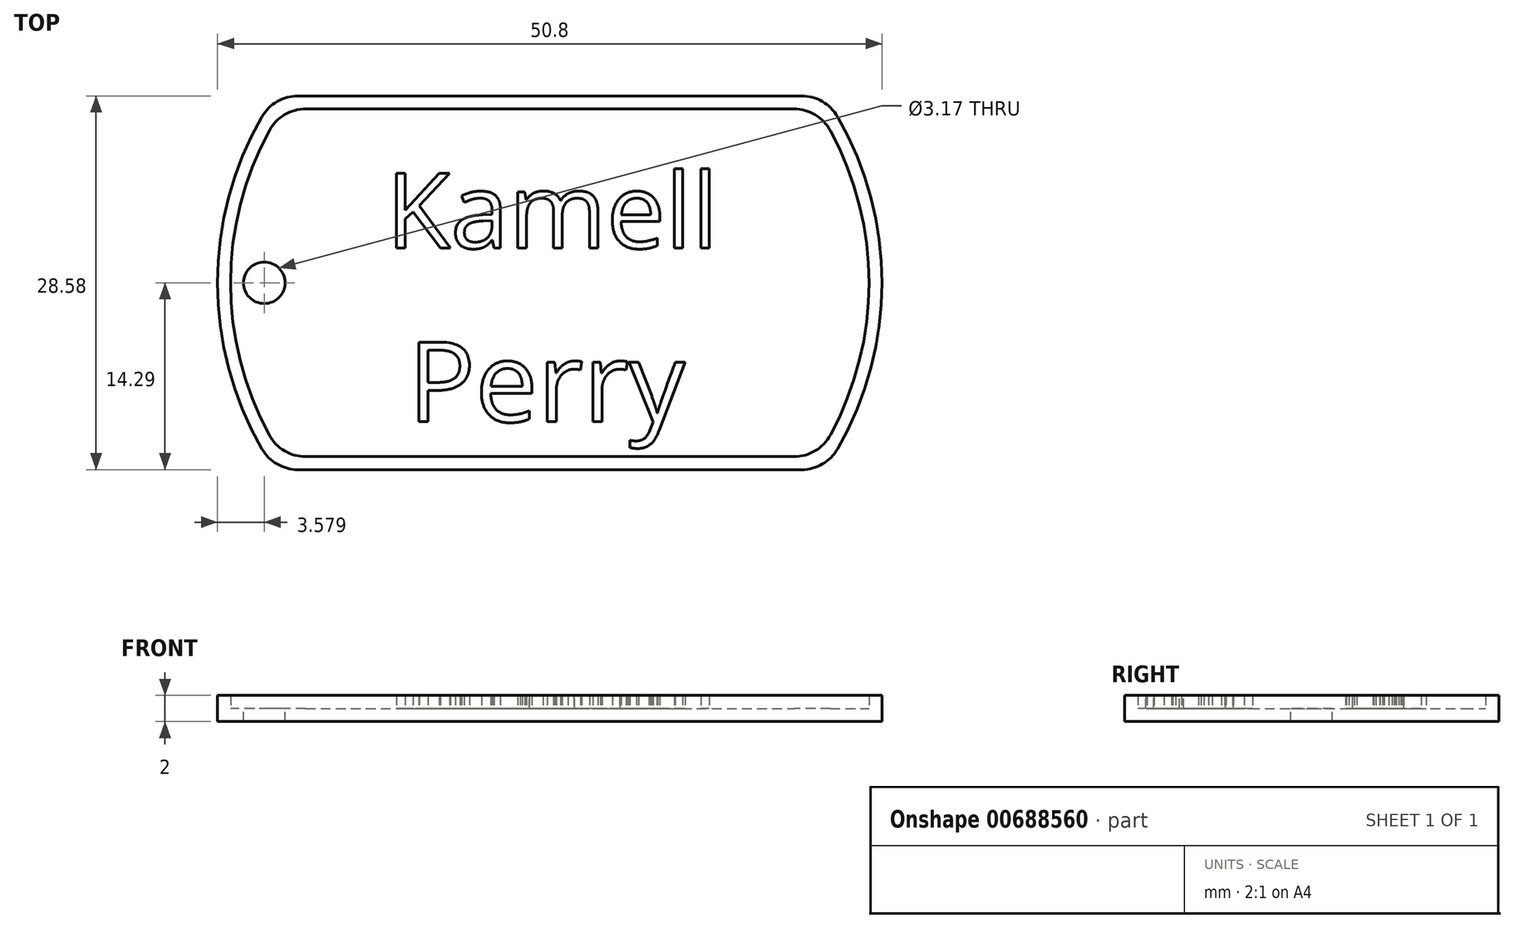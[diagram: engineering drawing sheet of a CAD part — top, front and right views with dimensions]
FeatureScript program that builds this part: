
annotation { "Feature Type Name" : "Feature", "Feature Type Description" : "" }
export const myFeature = defineFeature(function(context is Context, id is Id, definition is map)
    precondition{}
    {
        {
            var Q0;
            Q0=qCreatedBy(makeId("Top.planeOp"),FACE);
            var sketch = newSketch(context, id + "F0", { "sketchPlane" : qUnion([Q0])});
            skArc(sketch, "E0", {"start": v(-22, 12.7) * mm, "mid": v(-25.4, 0) * mm, "end": v(-22, -12.7) * mm});
            skLineSegment(sketch, "E1.top", {"start": v(-19.25, -14.29) * mm, "end": v(19.25, -14.29) * mm});
            skArc(sketch, "E2.trimOffspring", {"start": v(22, -12.7) * mm, "mid": v(25.4, 0) * mm, "end": v(22, 12.7) * mm});
            skLineSegment(sketch, "E3", {"start": v(-19.25, 14.29) * mm, "end": v(19.25, 14.29) * mm});
            skPoint(sketch, "E4.visualSharp", {"position": v(-21, 14.29) * mm});
            skArc(sketch, "E4.filletArc", {"start": v(-19.25, 14.29) * mm, "mid": v(-20.83, 13.86) * mm, "end": v(-22, 12.7) * mm});
            skPoint(sketch, "E5.visualSharp", {"position": v(21, 14.29) * mm});
            skArc(sketch, "E5.filletArc", {"start": v(22, 12.7) * mm, "mid": v(20.83, 13.86) * mm, "end": v(19.25, 14.29) * mm});
            skPoint(sketch, "E6.visualSharp", {"position": v(21, -14.29) * mm});
            skArc(sketch, "E6.filletArc", {"start": v(19.25, -14.29) * mm, "mid": v(20.83, -13.86) * mm, "end": v(22, -12.7) * mm});
            skPoint(sketch, "E7.visualSharp", {"position": v(-21, -14.29) * mm});
            skArc(sketch, "E7.filletArc", {"start": v(-22, -12.7) * mm, "mid": v(-20.83, -13.86) * mm, "end": v(-19.25, -14.29) * mm});
            skSolve(sketch);
        }
        {
            var Q0;
            Q0=makeQuery(id+"F0.imprint","IMPRINT",FACE,{"disambiguationData":[TD([[makeQuery(id+"F0.imprint","IMPRINT",EDGE,{"derivedFrom":sQuery(id+"F0.wireOp",EDGE,"E0")}),1.0]])]});
            extrude(context, id + "F1", {"entities" : qUnion([Q0]), "depth" : 1 * mm, "offsetDistance" : 25.4 * mm});
        }
        {
            var Q0;
            Q0=makeQuery(id+"F1.opExtrude","CAP_FACE",FACE,{"disambiguationData":[OSD([sQuery(id+"F0.wireOp",EDGE,"E0"),sQuery(id+"F0.wireOp",EDGE,"E1.top"),sQuery(id+"F0.wireOp",EDGE,"E2.trimOffspring"),sQuery(id+"F0.wireOp",EDGE,"E3"),sQuery(id+"F0.wireOp",EDGE,"E4.filletArc"),sQuery(id+"F0.wireOp",EDGE,"E5.filletArc"),sQuery(id+"F0.wireOp",EDGE,"E6.filletArc"),sQuery(id+"F0.wireOp",EDGE,"E7.filletArc")])],"isStart":false});
            var sketch = newSketch(context, id + "F2", { "sketchPlane" : qUnion([Q0])});
            skLineSegment(sketch, "E8.0", {"start": v(-18.66, 13.29) * mm, "end": v(18.66, 13.29) * mm});
            skArc(sketch, "E8.1", {"start": v(-21.45, 11.63) * mm, "mid": v(-24.4, 0) * mm, "end": v(-21.45, -11.63) * mm});
            skLineSegment(sketch, "E8.2", {"start": v(-18.66, -13.29) * mm, "end": v(18.66, -13.29) * mm});
            skArc(sketch, "E8.3", {"start": v(21.45, -11.63) * mm, "mid": v(24.4, 0) * mm, "end": v(21.45, 11.63) * mm});
            skPoint(sketch, "E9.visualSharp", {"position": v(-20.46, 13.29) * mm});
            skArc(sketch, "E9.filletArc", {"start": v(-18.66, 13.29) * mm, "mid": v(-20.29, 12.84) * mm, "end": v(-21.45, 11.63) * mm});
            skPoint(sketch, "E10.visualSharp", {"position": v(20.46, 13.29) * mm});
            skArc(sketch, "E10.filletArc", {"start": v(21.45, 11.63) * mm, "mid": v(20.29, 12.84) * mm, "end": v(18.66, 13.29) * mm});
            skPoint(sketch, "E11.visualSharp", {"position": v(20.46, -13.29) * mm});
            skArc(sketch, "E11.filletArc", {"start": v(18.66, -13.29) * mm, "mid": v(20.29, -12.84) * mm, "end": v(21.45, -11.63) * mm});
            skPoint(sketch, "E12.visualSharp", {"position": v(-20.46, -13.29) * mm});
            skArc(sketch, "E12.filletArc", {"start": v(-21.45, -11.63) * mm, "mid": v(-20.29, -12.84) * mm, "end": v(-18.66, -13.29) * mm});
            skLineSegment(sketch, "E13.0", {"start": v(-19.25, 14.29) * mm, "end": v(19.25, 14.29) * mm});
            skArc(sketch, "E13.1", {"start": v(-22, 12.7) * mm, "mid": v(-25.4, 0) * mm, "end": v(-22, -12.7) * mm});
            skLineSegment(sketch, "E13.2", {"start": v(-19.25, -14.29) * mm, "end": v(19.25, -14.29) * mm});
            skArc(sketch, "E13.3", {"start": v(22, -12.7) * mm, "mid": v(25.4, 0) * mm, "end": v(22, 12.7) * mm});
            skPoint(sketch, "E14.visualSharp", {"position": v(-21, -14.29) * mm});
            skArc(sketch, "E14.filletArc", {"start": v(-22, -12.7) * mm, "mid": v(-20.83, -13.86) * mm, "end": v(-19.25, -14.29) * mm});
            skPoint(sketch, "E15.visualSharp", {"position": v(21, -14.29) * mm});
            skArc(sketch, "E15.filletArc", {"start": v(19.25, -14.29) * mm, "mid": v(20.83, -13.86) * mm, "end": v(22, -12.7) * mm});
            skPoint(sketch, "E16.visualSharp", {"position": v(21, 14.29) * mm});
            skArc(sketch, "E16.filletArc", {"start": v(22, 12.7) * mm, "mid": v(20.83, 13.86) * mm, "end": v(19.25, 14.29) * mm});
            skPoint(sketch, "E17.visualSharp", {"position": v(-21, 14.29) * mm});
            skArc(sketch, "E17.filletArc", {"start": v(-19.25, 14.29) * mm, "mid": v(-20.83, 13.86) * mm, "end": v(-22, 12.7) * mm});
            skSolve(sketch);
        }
        {
            var Q0;
            Q0=makeQuery(id+"F2.imprint","IMPRINT",FACE,{"disambiguationData":[TD([[makeQuery(id+"F2.imprint","IMPRINT",EDGE,{"derivedFrom":sQuery(id+"F2.wireOp",EDGE,"E8.0")}),1.0]])]});
            extrude(context, id + "F3", {"entities" : qUnion([Q0]), "operationType" : NewBodyOperationType.ADD, "depth" : 1 * mm, "offsetDistance" : 25.4 * mm});
        }
        {
            var Q0;
            Q0=makeQuery(id+"F1.opExtrude","CAP_FACE",FACE,{"disambiguationData":[OSD([sQuery(id+"F0.wireOp",EDGE,"E0"),sQuery(id+"F0.wireOp",EDGE,"E1.top"),sQuery(id+"F0.wireOp",EDGE,"E2.trimOffspring"),sQuery(id+"F0.wireOp",EDGE,"E3"),sQuery(id+"F0.wireOp",EDGE,"E4.filletArc"),sQuery(id+"F0.wireOp",EDGE,"E5.filletArc"),sQuery(id+"F0.wireOp",EDGE,"E6.filletArc"),sQuery(id+"F0.wireOp",EDGE,"E7.filletArc")])],"isStart":false});
            var sketch = newSketch(context, id + "F4", { "sketchPlane" : qUnion([Q0])});
            skCircle(sketch, "E18", {"center": v(-21.82, 0) * mm, "radius": 1.59 * mm});
            skSolve(sketch);
        }
        {
            var Q0;
            Q0=makeQuery(id+"F4.imprint","IMPRINT",FACE,{"disambiguationData":[TD([[makeQuery(id+"F4.imprint","IMPRINT",EDGE,{"derivedFrom":sQuery(id+"F4.wireOp",EDGE,"E18")}),1.0]])]});
            extrude(context, id + "F5", {"entities" : qUnion([Q0]), "operationType" : NewBodyOperationType.REMOVE, "oppositeDirection" : true, "depth" : 1 * mm, "offsetDistance" : 25.4 * mm});
        }
        {
            var Q0;
            Q0=makeQuery(id+"F2.imprint","IMPRINT",FACE,{"disambiguationData":[TD([[makeQuery(id+"F2.imprint","IMPRINT",EDGE,{"derivedFrom":sQuery(id+"F2.wireOp",EDGE,"E8.0")}),-1.0]])]});
            var sketch = newSketch(context, id + "F6", { "sketchPlane" : qUnion([Q0])});
            skText(sketch, "E19", { "text": "Kamell", "fontName": "OpenSans-Regular.ttf"});
            const initialGuessF6  = {"E19": [-0.0125, 0.00265, 1, 0, 0.00577]};
            skSetInitialGuess(sketch, initialGuessF6);
            skSolve(sketch);
        }
        {
            var Q0;
            Q0=makeQuery(id+"F2.imprint","IMPRINT",FACE,{"disambiguationData":[TD([[makeQuery(id+"F2.imprint","IMPRINT",EDGE,{"derivedFrom":sQuery(id+"F2.wireOp",EDGE,"E8.0")}),-1.0]])]});
            var sketch = newSketch(context, id + "F7", { "sketchPlane" : qUnion([Q0])});
            skText(sketch, "E20", { "text": "Perry", "fontName": "OpenSans-Regular.ttf"});
            const initialGuessF7  = {"E20": [-0.01084, -0.01062, 1, 0, 0.00614]};
            skSetInitialGuess(sketch, initialGuessF7);
            skSolve(sketch);
        }
        {
            var Q0;
            Q0 = qSketchRegion(id + "F6", true);
            extrude(context, id + "F8", {"entities" : qUnion([Q0]), "operationType" : NewBodyOperationType.ADD, "depth" : 1 * mm, "offsetDistance" : 25.4 * mm});
        }
        {
            var Q0;
            Q0 = qSketchRegion(id + "F7", true);
            extrude(context, id + "F9", {"entities" : qUnion([Q0]), "operationType" : NewBodyOperationType.ADD, "depth" : 1 * mm, "offsetDistance" : 25.4 * mm});
        }
    });
